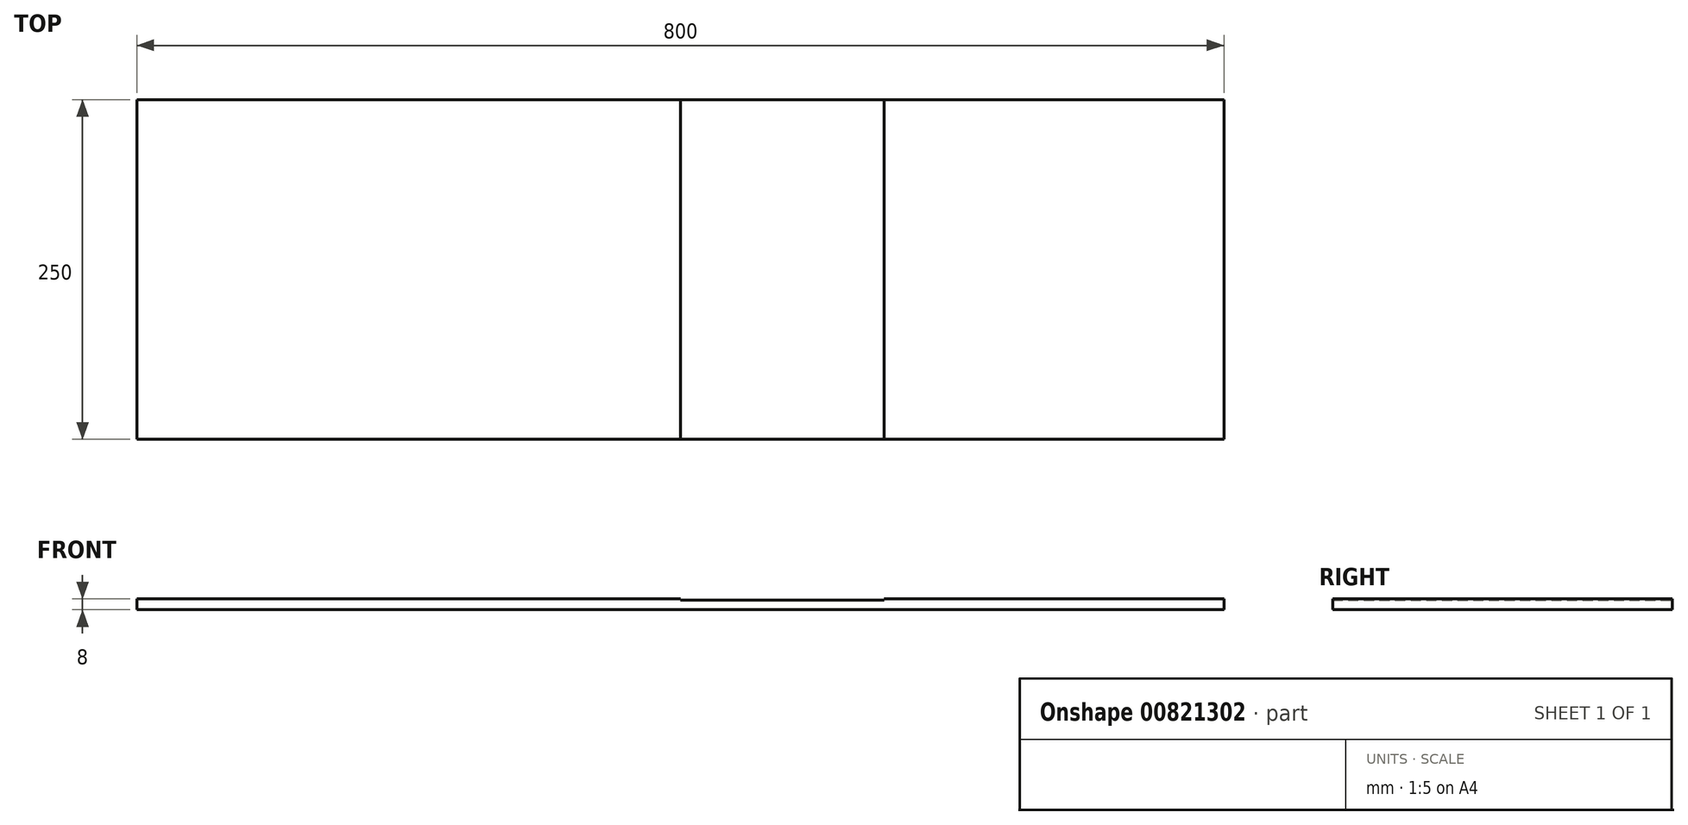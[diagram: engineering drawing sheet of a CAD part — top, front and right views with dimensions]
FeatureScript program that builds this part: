
annotation { "Feature Type Name" : "Feature", "Feature Type Description" : "" }
export const myFeature = defineFeature(function(context is Context, id is Id, definition is map)
    precondition{}
    {
        {
            var Q0;
            Q0=qCreatedBy(makeId("Front.planeOp"),FACE);
            var sketch = newSketch(context, id + "F0", { "sketchPlane" : qUnion([Q0])});
            skLineSegment(sketch, "E0", {"start": v(-225, 8) * mm, "end": v(575, 8) * mm});
            skLineSegment(sketch, "E1", {"start": v(575, 0) * mm, "end": v(-225, 0) * mm});
            skLineSegment(sketch, "E2", {"start": v(-225, 0) * mm, "end": v(-225, 8) * mm});
            skLineSegment(sketch, "E3", {"start": v(575, 0) * mm, "end": v(575, 8) * mm});
            skPoint(sketch, "E4", {"position": v(0, 0) * mm});
            skPoint(sketch, "E5", {"position": v(0, 8) * mm});
            skSolve(sketch);
        }
        {
            var Q0;
            Q0=qCreatedBy(makeId("Front.planeOp"),FACE);
            var sketch = newSketch(context, id + "F1", { "sketchPlane" : qUnion([Q0])});
            skLineSegment(sketch, "E6", {"start": v(175, 8) * mm, "end": v(175, 7) * mm});
            skLineSegment(sketch, "E7", {"start": v(250, 8) * mm, "end": v(175, 8) * mm});
            skLineSegment(sketch, "E8", {"start": v(175, 7) * mm, "end": v(250, 7) * mm});
            skLineSegment(sketch, "E9", {"start": v(250, 7) * mm, "end": v(250, 8) * mm, "construction": true});
            skLineSegment(sketch, "E10.MirrorCS", {"start": v(325, 8) * mm, "end": v(325, 7) * mm});
            skLineSegment(sketch, "E11.MirrorCS", {"start": v(250, 8) * mm, "end": v(325, 8) * mm});
            skLineSegment(sketch, "E12.MirrorCS", {"start": v(325, 7) * mm, "end": v(250, 7) * mm});
            skSolve(sketch);
        }
        {
            var Q0;
            Q0=qSketchRegion(id+"F0",true);
            extrude(context, id + "F2", {"entities" : qUnion([Q0]), "endBound" : BoundingType.SYMMETRIC, "oppositeDirection" : true, "depth" : 250 * mm, "offsetDistance" : 25 * mm});
        }
        {
            var Q0;
            Q0=qSketchRegion(id+"F1",true);
            var Q1;
            Q1=makeQuery(id+"F2.opExtrude","CAP_FACE",FACE,{"disambiguationData":[OSD([sQuery(id+"F0.wireOp",EDGE,"E0"),sQuery(id+"F0.wireOp",EDGE,"E1"),sQuery(id+"F0.wireOp",EDGE,"E2"),sQuery(id+"F0.wireOp",EDGE,"E3")])],"isStart":true});
            extrude(context, id + "F3", {"entities" : qUnion([Q0]), "operationType" : NewBodyOperationType.REMOVE, "endBound" : BoundingType.THROUGH_ALL, "depth" : 25 * mm, "endBoundEntityFace" : qUnion([Q1]), "offsetDistance" : 25 * mm});
        }
        {
            var Q0;
            Q0=qSketchRegion(id+"F1",true);
            extrude(context, id + "F4", {"entities" : qUnion([Q0]), "operationType" : NewBodyOperationType.REMOVE, "endBound" : BoundingType.THROUGH_ALL, "oppositeDirection" : true, "depth" : 25 * mm, "offsetDistance" : 25 * mm});
        }
    });
